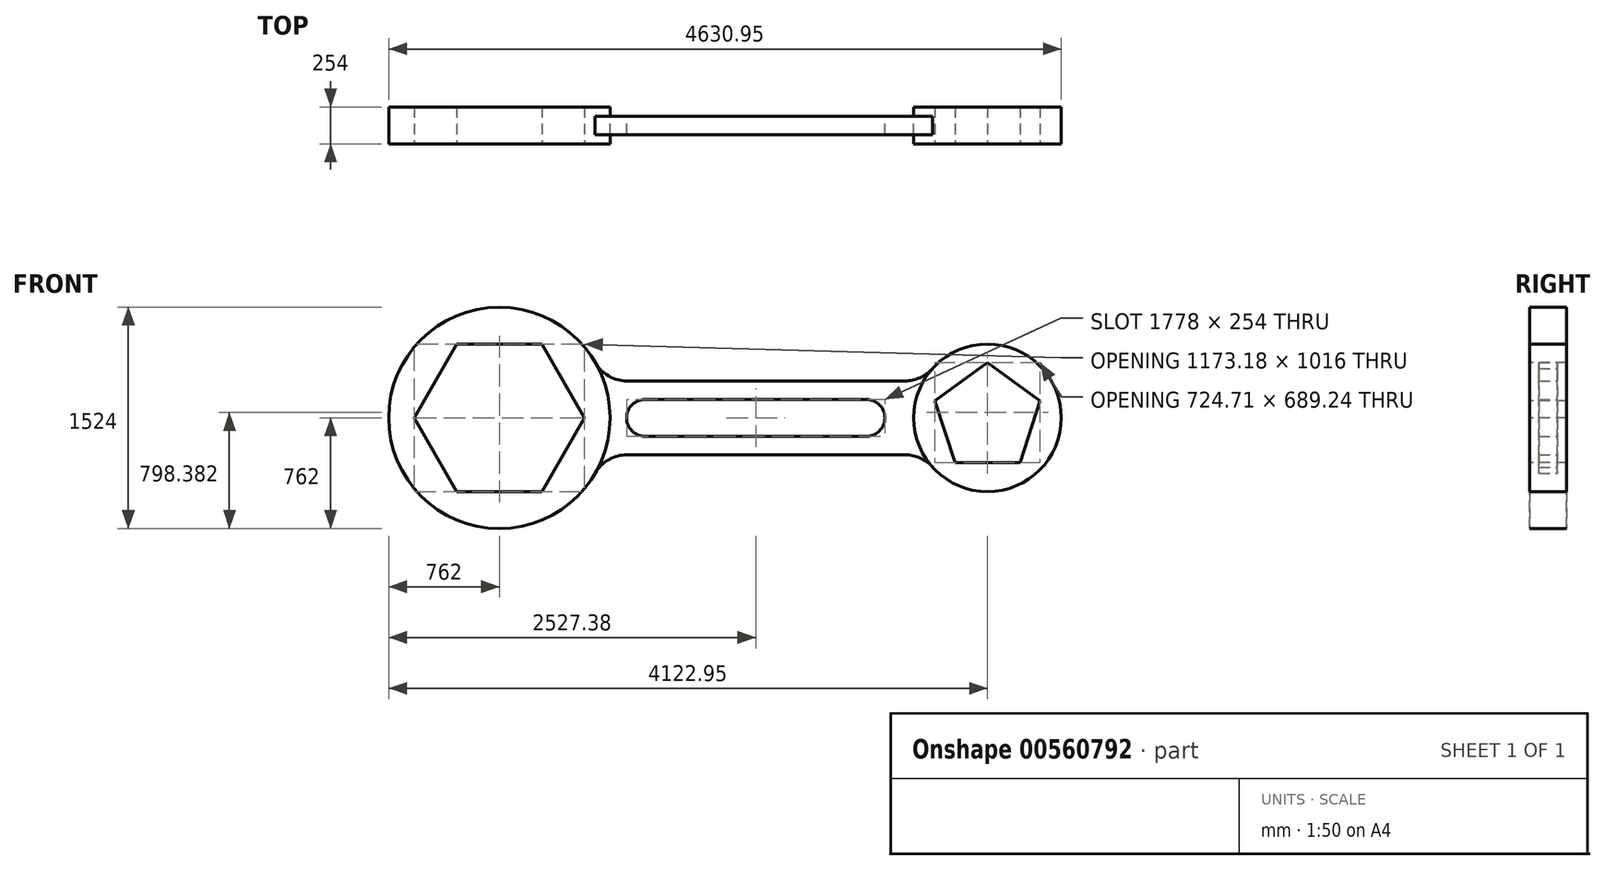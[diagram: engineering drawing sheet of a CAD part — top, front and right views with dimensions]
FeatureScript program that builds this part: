
annotation { "Feature Type Name" : "Feature", "Feature Type Description" : "" }
export const myFeature = defineFeature(function(context is Context, id is Id, definition is map)
    precondition{}
    {
        {
            var Q0;
            Q0=qCreatedBy(makeId("Front.planeOp"),FACE);
            var sketch = newSketch(context, id + "F0", { "sketchPlane" : qUnion([Q0])});
            skCircle(sketch, "E0", {"center": v(0, 0) * mm, "radius": 762 * mm});
            skCircle(sketch, "E1", {"center": v(3360.95, 0) * mm, "radius": 508 * mm});
            skPoint(sketch, "E2.startSnap0", {"position": v(1807.48, 0) * mm});
            skLineSegment(sketch, "E3", {"start": v(1765.38, 127) * mm, "end": v(1003.38, 127) * mm});
            skLineSegment(sketch, "E4", {"start": v(1003.38, -127) * mm, "end": v(2527.38, -127) * mm});
            skLineSegment(sketch, "E5", {"start": v(2527.38, 127) * mm, "end": v(1765.38, 127) * mm});
            skLineSegment(sketch, "E6", {"start": v(2793, -254) * mm, "end": v(879.88, -254) * mm});
            skLineSegment(sketch, "E7", {"start": v(2793, 254) * mm, "end": v(879.88, 254) * mm});
            skPoint(sketch, "E8.orphan", {"position": v(1849.57, 254) * mm});
            skPoint(sketch, "E9.orphan", {"position": v(1849.57, -254) * mm});
            skArc(sketch, "E10", {"start": v(1003.38, 127) * mm, "mid": v(876.38, 0) * mm, "end": v(1003.38, -127) * mm});
            skArc(sketch, "E11", {"start": v(2527.38, -127) * mm, "mid": v(2654.38, 0) * mm, "end": v(2527.38, 127) * mm});
            skPoint(sketch, "E12.orphan", {"position": v(876.38, 127) * mm});
            skPoint(sketch, "E13.orphan", {"position": v(2654.38, 127) * mm});
            skArc(sketch, "E14", {"start": v(659.91, 381) * mm, "mid": v(752.88, 288.03) * mm, "end": v(879.88, 254) * mm});
            skArc(sketch, "E15", {"start": v(879.88, -254) * mm, "mid": v(752.88, -288.03) * mm, "end": v(659.91, -381) * mm});
            skArc(sketch, "E16", {"start": v(2793, 254) * mm, "mid": v(2896.69, 276.13) * mm, "end": v(2982.31, 338.67) * mm});
            skArc(sketch, "E17", {"start": v(2982.31, -338.67) * mm, "mid": v(2896.69, -276.13) * mm, "end": v(2793, -254) * mm});
            skPoint(sketch, "E18.orphan", {"position": v(2921.01, -254) * mm});
            skPoint(sketch, "E19.orphan", {"position": v(2921.01, 254) * mm});
            skPoint(sketch, "E20.orphan", {"position": v(762, 0) * mm});
            skPoint(sketch, "E21.orphan", {"position": v(2852.95, 0) * mm});
            skCircle(sketch, "E22.cCircle", {"center": v(0, 0) * mm, "radius": 508 * mm, "construction": true});
            skLineSegment(sketch, "E22.0", {"start": v(-293.3, 508) * mm, "end": v(293.3, 508) * mm});
            skLineSegment(sketch, "E22.1", {"start": v(293.3, 508) * mm, "end": v(586.59, 0) * mm});
            skLineSegment(sketch, "E22.2", {"start": v(586.59, 0) * mm, "end": v(293.3, -508) * mm});
            skLineSegment(sketch, "E22.3", {"start": v(293.3, -508) * mm, "end": v(-293.3, -508) * mm});
            skLineSegment(sketch, "E22.4", {"start": v(-293.3, -508) * mm, "end": v(-586.59, 0) * mm});
            skLineSegment(sketch, "E22.5", {"start": v(-586.59, 0) * mm, "end": v(-293.3, 508) * mm});
            skPoint(sketch, "E22.0.midPoint", {"position": v(0, 508) * mm});
            skCircle(sketch, "E23.cCircle", {"center": v(3360.95, 0) * mm, "radius": 308.24 * mm, "construction": true});
            skLineSegment(sketch, "E23.0", {"start": v(3584.9, -308.24) * mm, "end": v(3137, -308.24) * mm});
            skLineSegment(sketch, "E23.1", {"start": v(3137, -308.24) * mm, "end": v(2998.6, 117.74) * mm});
            skLineSegment(sketch, "E23.2", {"start": v(2998.6, 117.74) * mm, "end": v(3360.95, 381) * mm});
            skLineSegment(sketch, "E23.3", {"start": v(3360.95, 381) * mm, "end": v(3723.3, 117.74) * mm});
            skLineSegment(sketch, "E23.4", {"start": v(3723.3, 117.74) * mm, "end": v(3584.9, -308.24) * mm});
            skPoint(sketch, "E23.0.midPoint", {"position": v(3360.95, -308.24) * mm});
            skSolve(sketch);
        }
        {
            var Q0;
            Q0=makeQuery(id+"F0.imprint","IMPRINT",FACE,{"disambiguationData":[TD([[makeQuery(id+"F0.imprint","IMPRINT",EDGE,{"derivedFrom":sQuery(id+"F0.wireOp",EDGE,"E22.0")}),1.0]])]});
            var Q1;
            Q1=makeQuery(id+"F0.imprint","IMPRINT",FACE,{"disambiguationData":[TD([[makeQuery(id+"F0.imprint","IMPRINT",EDGE,{"derivedFrom":sQuery(id+"F0.wireOp",EDGE,"E23.0")}),1.0]])]});
            extrude(context, id + "F1", {"entities" : qUnion([Q0, Q1]), "oppositeDirection" : true, "depth" : 254 * mm, "offsetDistance" : 25.4 * mm, "symmetric" : true});
        }
        {
            var Q0;
            Q0=makeQuery(id+"F0.imprint","IMPRINT",FACE,{"disambiguationData":[TD([[makeQuery(id+"F0.imprint","IMPRINT",EDGE,{"derivedFrom":sQuery(id+"F0.wireOp",EDGE,"E3")}),-1.0]])]});
            extrude(context, id + "F2", {"entities" : qUnion([Q0]), "depth" : 127 * mm, "offsetDistance" : 25.4 * mm, "symmetric" : true});
        }
    });
